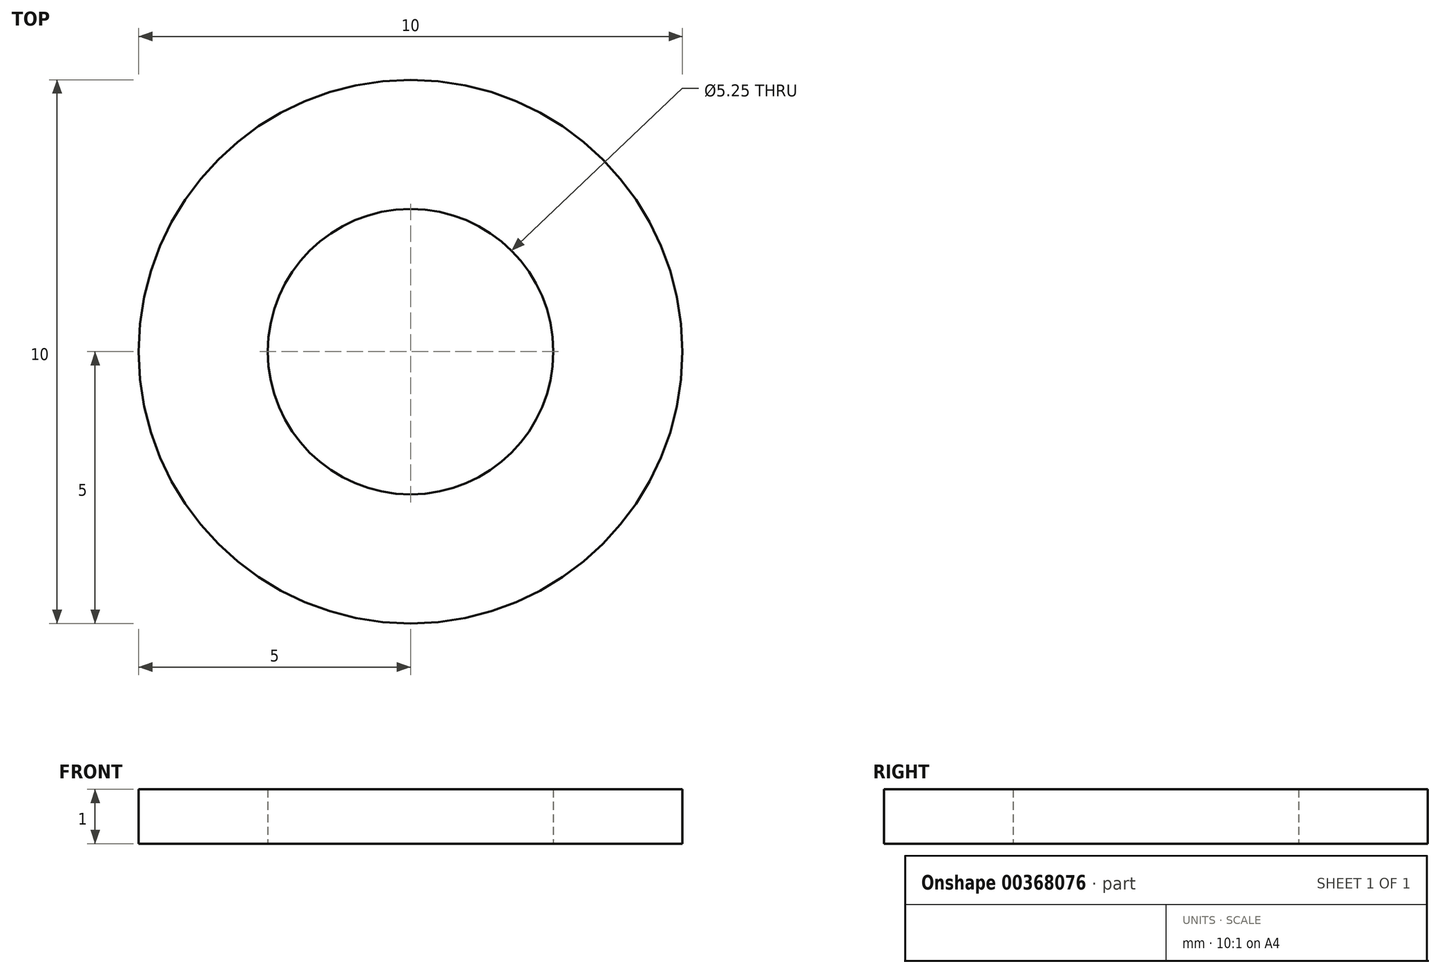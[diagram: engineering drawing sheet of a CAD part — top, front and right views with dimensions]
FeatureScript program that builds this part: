
annotation { "Feature Type Name" : "Feature", "Feature Type Description" : "" }
export const myFeature = defineFeature(function(context is Context, id is Id, definition is map)
    precondition{}
    {
        {
            var Q0;
            Q0=qCreatedBy(makeId("Top.planeOp"),FACE);
            var sketch = newSketch(context, id + "F0", { "sketchPlane" : qUnion([Q0])});
            skCircle(sketch, "E0", {"center": v(0, 0) * mm, "radius": 5 * mm});
            skCircle(sketch, "E1", {"center": v(0, 0) * mm, "radius": 2.62 * mm});
            skSolve(sketch);
        }
        {
            var Q0;
            Q0=makeQuery(id+"F0.imprint","IMPRINT",FACE,{"disambiguationData":[TD([[makeQuery(id+"F0.imprint","IMPRINT",EDGE,{"derivedFrom":sQuery(id+"F0.wireOp",EDGE,"E0")}),1.0]])]});
            extrude(context, id + "F1", {"entities" : qUnion([Q0]), "depth" : 1 * mm});
        }
    });
